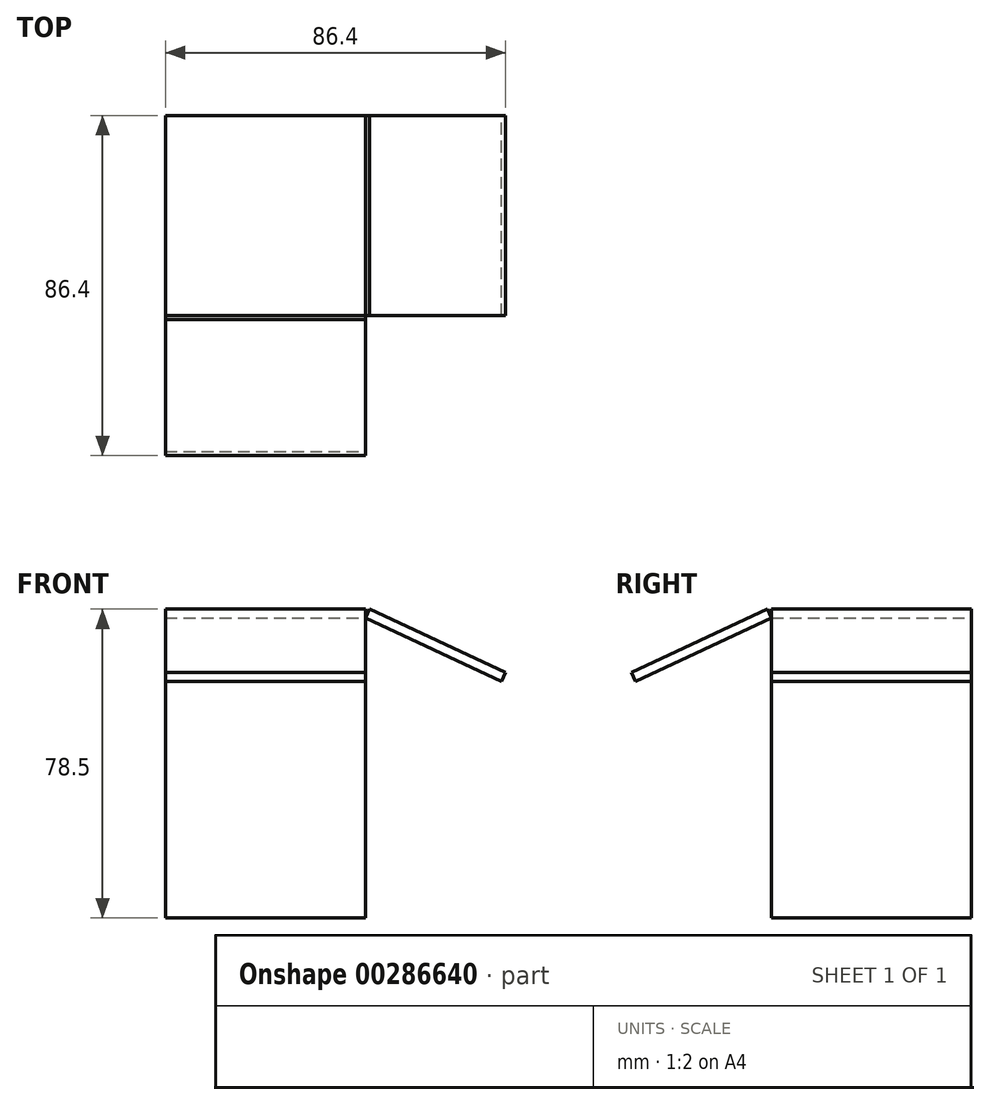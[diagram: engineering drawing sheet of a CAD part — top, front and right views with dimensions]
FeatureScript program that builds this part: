
annotation { "Feature Type Name" : "Feature", "Feature Type Description" : "" }
export const myFeature = defineFeature(function(context is Context, id is Id, definition is map)
    precondition{}
    {
        {
            var Q0;
            Q0=qCreatedBy(makeId("Front.planeOp"),FACE);
            var sketch = newSketch(context, id + "F0", { "sketchPlane" : qUnion([Q0])});
            skLineSegment(sketch, "E0.bottom", {"start": v(25.4, 38.1) * mm, "end": v(-25.4, 38.1) * mm});
            skLineSegment(sketch, "E0.top", {"start": v(25.4, -38.1) * mm, "end": v(-25.4, -38.1) * mm});
            skLineSegment(sketch, "E0.left", {"start": v(25.4, 38.1) * mm, "end": v(25.4, -38.1) * mm});
            skLineSegment(sketch, "E0.right", {"start": v(-25.4, 38.1) * mm, "end": v(-25.4, -38.1) * mm});
            skPoint(sketch, "E0.middle", {"position": v(0, 0) * mm});
            skSolve(sketch);
        }
        {
            var Q0;
            Q0 = qSketchRegion(id + "F0", true);
            extrude(context, id + "F1", {"entities" : qUnion([Q0]), "endBound" : BoundingType.SYMMETRIC, "depth" : 50.8 * mm});
        }
        {
            var Q0;
            Q0=makeQuery(id+"F1.opExtrude","CAP_EDGE",EDGE,{"disambiguationData":[OSD([sQuery(id+"F0.wireOp",EDGE,"E0.bottom")])],"isStart":false});
            cPlane(context, id + "F2", {"entities" : qUnion([Q0]), "cplaneType" : CPlaneType.LINE_ANGLE, "offset" : 25.4 * mm, "angle" : 65 * degree, "width" : 152.4 * mm, "height" : 152.4 * mm});
        }
        {
            var Q0;
            Q0=makeQuery(id+"F1.opExtrude","SWEPT_EDGE",EDGE,{"disambiguationData":[OSD([sQuery(id+"F0.wireOp",EDGE,"E0.bottom"),sQuery(id+"F0.wireOp",EDGE,"E0.left")])]});
            cPlane(context, id + "F3", {"entities" : qUnion([Q0]), "cplaneType" : CPlaneType.LINE_ANGLE, "offset" : 25.4 * mm, "angle" : 25 * degree, "width" : 152.4 * mm, "height" : 152.4 * mm});
        }
        {
            var Q0;
            Q0=qCreatedBy(id+"F2.planeOp",FACE);
            var sketch = newSketch(context, id + "F4", { "sketchPlane" : qUnion([Q0])});
            skLineSegment(sketch, "E1.bottom", {"start": v(-25.4, -6.92) * mm, "end": v(25.4, -6.92) * mm});
            skLineSegment(sketch, "E1.top", {"start": v(-25.4, -45.02) * mm, "end": v(25.4, -45.02) * mm});
            skLineSegment(sketch, "E1.left", {"start": v(-25.4, -6.92) * mm, "end": v(-25.4, -45.02) * mm});
            skLineSegment(sketch, "E1.right", {"start": v(25.4, -6.92) * mm, "end": v(25.4, -45.02) * mm});
            skSolve(sketch);
        }
        {
            var Q0;
            Q0=makeQuery(id+"F4.imprint","IMPRINT",FACE,{"disambiguationData":[TD([[makeQuery(id+"F4.imprint","IMPRINT",EDGE,{"derivedFrom":sQuery(id+"F4.wireOp",EDGE,"E1.bottom")}),-1.0]])]});
            extrude(context, id + "F5", {"entities" : qUnion([Q0]), "operationType" : NewBodyOperationType.ADD, "depth" : 2.54 * mm});
        }
        {
            var Q0;
            Q0=qCreatedBy(id+"F3.planeOp",FACE);
            var sketch = newSketch(context, id + "F6", { "sketchPlane" : qUnion([Q0])});
            skLineSegment(sketch, "E2.bottom", {"start": v(6.92, -25.4) * mm, "end": v(45.02, -25.4) * mm});
            skLineSegment(sketch, "E2.top", {"start": v(6.92, 25.4) * mm, "end": v(45.02, 25.4) * mm});
            skLineSegment(sketch, "E2.left", {"start": v(6.92, -25.4) * mm, "end": v(6.92, 25.4) * mm});
            skLineSegment(sketch, "E2.right", {"start": v(45.02, -25.4) * mm, "end": v(45.02, 25.4) * mm});
            skSolve(sketch);
        }
        {
            var Q0;
            Q0 = qSketchRegion(id + "F6", true);
            extrude(context, id + "F7", {"entities" : qUnion([Q0]), "depth" : 2.54 * mm});
        }
    });
